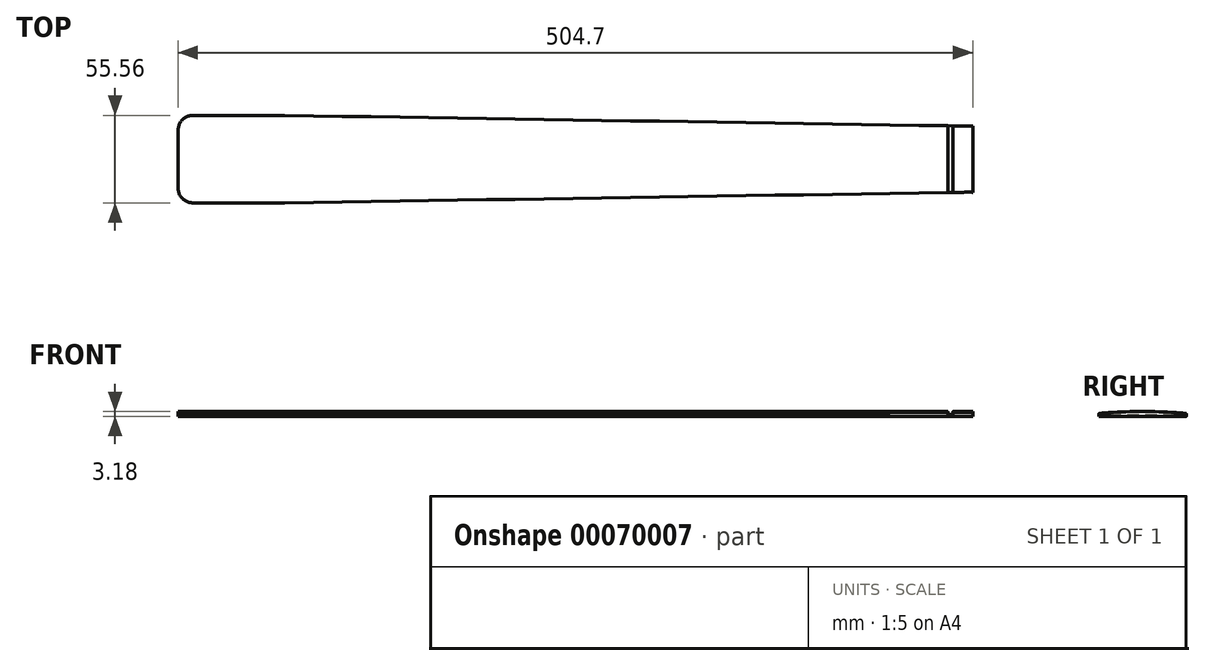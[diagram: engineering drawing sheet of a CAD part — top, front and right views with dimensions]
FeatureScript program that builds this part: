
annotation { "Feature Type Name" : "Feature", "Feature Type Description" : "" }
export const myFeature = defineFeature(function(context is Context, id is Id, definition is map)
    precondition{}
    {
        {
            var Q0;
            Q0=qCreatedBy(makeId("Top.planeOp"),FACE);
            var sketch = newSketch(context, id + "F0", { "sketchPlane" : qUnion([Q0])});
            skCircle(sketch, "E0", {"center": v(292.26, -12.07) * mm, "radius": 1.59 * mm});
            skCircle(sketch, "E1", {"center": v(256.89, 21.35) * mm, "radius": 1.59 * mm});
            skArc(sketch, "E2", {"start": v(-264.91, -27.78) * mm, "mid": v(-263.92, -27.78) * mm, "end": v(-262.93, -27.77) * mm});
            skLineSegment(sketch, "E3", {"start": v(171.05, -21) * mm, "end": v(-262.93, -27.77) * mm});
            skLineSegment(sketch, "E4", {"start": v(331.4, -12.7) * mm, "end": v(331.4, 12.7) * mm});
            skArc(sketch, "E5", {"start": v(171.05, -21) * mm, "mid": v(193.16, -26.95) * mm, "end": v(208.81, -43.66) * mm});
            skCircle(sketch, "E6", {"center": v(292.26, 12.07) * mm, "radius": 1.59 * mm});
            skLineSegment(sketch, "E7", {"start": v(208.81, 43.66) * mm, "end": v(234.21, 43.66) * mm});
            skLineSegment(sketch, "E8", {"start": v(234.21, 43.66) * mm, "end": v(331.4, 12.7) * mm});
            skLineSegment(sketch, "E9", {"start": v(-262.93, 27.77) * mm, "end": v(171.05, 21) * mm});
            skCircle(sketch, "E10", {"center": v(221.51, 30.63) * mm, "radius": 1.59 * mm});
            skArc(sketch, "E11", {"start": v(-321.07, 27.78) * mm, "mid": v(-327.8, 25) * mm, "end": v(-330.6, 18.26) * mm});
            skLineSegment(sketch, "E12", {"start": v(133.75, 3.18) * mm, "end": v(-296.47, 3.18) * mm});
            skCircle(sketch, "E13", {"center": v(221.51, -30.63) * mm, "radius": 1.59 * mm});
            skLineSegment(sketch, "E14", {"start": v(-264.91, 27.78) * mm, "end": v(-321.07, 27.78) * mm});
            skLineSegment(sketch, "E15", {"start": v(-330.6, 18.26) * mm, "end": v(-330.6, -18.26) * mm});
            skLineSegment(sketch, "E16", {"start": v(234.21, -43.66) * mm, "end": v(331.4, -12.7) * mm});
            skArc(sketch, "E17", {"start": v(-330.6, -18.26) * mm, "mid": v(-327.8, -25) * mm, "end": v(-321.07, -27.78) * mm});
            skLineSegment(sketch, "E18", {"start": v(133.75, -3.18) * mm, "end": v(133.75, 3.18) * mm});
            skArc(sketch, "E19", {"start": v(-262.93, 27.77) * mm, "mid": v(-263.92, 27.78) * mm, "end": v(-264.91, 27.78) * mm});
            skLineSegment(sketch, "E20", {"start": v(-331.4, 4.76) * mm, "end": v(-296.47, 4.76) * mm});
            skCircle(sketch, "E21", {"center": v(256.89, -21.35) * mm, "radius": 1.59 * mm});
            skLineSegment(sketch, "E22", {"start": v(-296.47, -3.18) * mm, "end": v(133.75, -3.18) * mm});
            skLineSegment(sketch, "E23", {"start": v(-331.4, 4.76) * mm, "end": v(-331.4, -4.76) * mm});
            skLineSegment(sketch, "E24", {"start": v(-331.4, -4.76) * mm, "end": v(-296.47, -4.76) * mm});
            skLineSegment(sketch, "E25", {"start": v(-296.47, -4.76) * mm, "end": v(-296.47, -3.18) * mm});
            skLineSegment(sketch, "E26", {"start": v(-296.47, 3.18) * mm, "end": v(-296.47, 4.76) * mm});
            skArc(sketch, "E27", {"start": v(171.05, 21) * mm, "mid": v(193.16, 26.95) * mm, "end": v(208.81, 43.66) * mm});
            skLineSegment(sketch, "E28", {"start": v(-264.91, -27.78) * mm, "end": v(-321.07, -27.78) * mm});
            skLineSegment(sketch, "E29", {"start": v(208.81, -43.66) * mm, "end": v(234.21, -43.66) * mm});
            skSolve(sketch);
        }
        {
            var Q0;
            Q0=qCreatedBy(makeId("Top.planeOp"),FACE);
            var sketch = newSketch(context, id + "F1", { "sketchPlane" : qUnion([Q0])});
            skArc(sketch, "E30.2", {"start": v(-264.91, -27.78) * mm, "mid": v(-263.92, -27.78) * mm, "end": v(-262.93, -27.77) * mm});
            skLineSegment(sketch, "E30.3", {"start": v(171.05, -21) * mm, "end": v(-262.93, -27.77) * mm});
            skLineSegment(sketch, "E30.9", {"start": v(-262.93, 27.77) * mm, "end": v(171.05, 21) * mm});
            skArc(sketch, "E30.11", {"start": v(-321.07, 27.78) * mm, "mid": v(-327.8, 25) * mm, "end": v(-330.6, 18.26) * mm});
            skLineSegment(sketch, "E30.14", {"start": v(-264.91, 27.78) * mm, "end": v(-321.07, 27.78) * mm});
            skLineSegment(sketch, "E30.15", {"start": v(-330.6, 18.26) * mm, "end": v(-330.6, -18.26) * mm});
            skArc(sketch, "E30.17", {"start": v(-330.6, -18.26) * mm, "mid": v(-327.8, -25) * mm, "end": v(-321.07, -27.78) * mm});
            skArc(sketch, "E30.19", {"start": v(-262.93, 27.77) * mm, "mid": v(-263.92, 27.78) * mm, "end": v(-264.91, 27.78) * mm});
            skLineSegment(sketch, "E30.28", {"start": v(-264.91, -27.78) * mm, "end": v(-321.07, -27.78) * mm});
            skLineSegment(sketch, "E31", {"start": v(171.05, 21) * mm, "end": v(171.05, -21) * mm, "construction": true});
            skArc(sketch, "E32.0", {"start": v(171.05, -21) * mm, "mid": v(193.16, -26.95) * mm, "end": v(208.81, -43.66) * mm});
            skArc(sketch, "E32.1", {"start": v(171.05, 21) * mm, "mid": v(193.16, 26.95) * mm, "end": v(208.81, 43.66) * mm});
            skLineSegment(sketch, "E33", {"start": v(208.81, -43.66) * mm, "end": v(208.81, 43.66) * mm});
            skSolve(sketch);
        }
        {
            var Q0;
            Q0 = qSketchRegion(id + "F1", true);
            extrude(context, id + "F2", {"entities" : qUnion([Q0]), "depth" : 3.8 * mm});
        }
        {
            var Q0;
            Q0=makeQuery(id+"F2.opExtrude","CAP_FACE",FACE,{"disambiguationData":[OSD([sQuery(id+"F1.wireOp",EDGE,"E30.2"),sQuery(id+"F1.wireOp",EDGE,"E30.3"),sQuery(id+"F1.wireOp",EDGE,"E30.9"),sQuery(id+"F1.wireOp",EDGE,"E30.11"),sQuery(id+"F1.wireOp",EDGE,"E30.14"),sQuery(id+"F1.wireOp",EDGE,"E30.15"),sQuery(id+"F1.wireOp",EDGE,"E30.17"),sQuery(id+"F1.wireOp",EDGE,"E30.19"),sQuery(id+"F1.wireOp",EDGE,"E30.28"),sQuery(id+"F1.wireOp",EDGE,"E32.0"),sQuery(id+"F1.wireOp",EDGE,"E32.1"),sQuery(id+"F1.wireOp",EDGE,"E33")])],"isStart":false});
            var sketch = newSketch(context, id + "F3", { "sketchPlane" : qUnion([Q0])});
            skLineSegment(sketch, "E34.bottom", {"start": v(161.4, -25.4) * mm, "end": v(158.35, -25.4) * mm});
            skLineSegment(sketch, "E34.top", {"start": v(161.4, 25.4) * mm, "end": v(158.35, 25.4) * mm});
            skLineSegment(sketch, "E34.left", {"start": v(161.4, -25.4) * mm, "end": v(161.4, 25.4) * mm});
            skLineSegment(sketch, "E34.right", {"start": v(158.35, -25.4) * mm, "end": v(158.35, 25.4) * mm});
            skPoint(sketch, "E34.middle", {"position": v(159.88, 0) * mm});
            skLineSegment(sketch, "E35", {"start": v(-489.35, 622.32) * mm, "end": v(-489.35, -872.8) * mm, "construction": true});
            skSolve(sketch);
        }
        {
            var Q0;
            Q0 = qSketchRegion(id + "F3", true);
            extrude(context, id + "F4", {"entities" : qUnion([Q0]), "operationType" : NewBodyOperationType.REMOVE, "oppositeDirection" : true, "depth" : 2.38 * mm});
        }
        {
            var Q0;
            Q0=qCreatedBy(makeId("Right.planeOp"),FACE);
            var sketch = newSketch(context, id + "F5", { "sketchPlane" : qUnion([Q0])});
            skLineSegment(sketch, "E36", {"start": v(0, 15.88) * mm, "end": v(-38.1, 15.87) * mm});
            skLineSegment(sketch, "E37", {"start": v(-38.1, 15.87) * mm, "end": v(-38.1, 0.78) * mm});
            skLineSegment(sketch, "E38", {"start": v(0, 110.67) * mm, "end": v(0, 3.17) * mm, "construction": true});
            skLineSegment(sketch, "E39", {"start": v(0, 3.17) * mm, "end": v(58.07, 3.18) * mm, "construction": true});
            skArc(sketch, "E40", {"start": v(0, 3.17) * mm, "mid": v(-19.09, 2.58) * mm, "end": v(-38.1, 0.78) * mm});
            skLineSegment(sketch, "E41.MirrorCS", {"start": v(0, 15.88) * mm, "end": v(38.1, 15.87) * mm});
            skLineSegment(sketch, "E42.MirrorCS", {"start": v(38.1, 15.87) * mm, "end": v(38.1, 0.78) * mm});
            skArc(sketch, "E43.MirrorCS", {"start": v(0, 3.17) * mm, "mid": v(19.09, 2.58) * mm, "end": v(38.1, 0.78) * mm});
            skSolve(sketch);
        }
        {
            var Q0;
            Q0 = qSketchRegion(id + "F5", true);
            extrude(context, id + "F6", {"entities" : qUnion([Q0]), "operationType" : NewBodyOperationType.REMOVE, "endBound" : BoundingType.THROUGH_ALL, "oppositeDirection" : true, "depth" : 25.4 * mm, "hasSecondDirection" : true, "secondDirectionBound" : BoundingType.THROUGH_ALL, "secondDirectionOppositeDirection" : false, "secondDirectionDepth" : 25.4 * mm});
        }
        {
            var Q0;
            Q0=qCreatedBy(makeId("Top.planeOp"),FACE);
            var sketch = newSketch(context, id + "F7", { "sketchPlane" : qUnion([Q0])});
            skLineSegment(sketch, "E44.bottom", {"start": v(237.6, -63.5) * mm, "end": v(174.1, -63.5) * mm});
            skLineSegment(sketch, "E44.top", {"start": v(237.6, 63.5) * mm, "end": v(174.1, 63.5) * mm});
            skLineSegment(sketch, "E44.left", {"start": v(237.6, -63.5) * mm, "end": v(237.6, 63.5) * mm});
            skLineSegment(sketch, "E44.right", {"start": v(174.1, -63.5) * mm, "end": v(174.1, 63.5) * mm});
            skPoint(sketch, "E44.middle", {"position": v(205.85, 0) * mm});
            skSolve(sketch);
        }
        {
            var Q0;
            Q0 = qSketchRegion(id + "F7", true);
            extrude(context, id + "F8", {"entities" : qUnion([Q0]), "operationType" : NewBodyOperationType.REMOVE, "endBound" : BoundingType.THROUGH_ALL, "depth" : 25.4 * mm});
        }
    });
